# Revit family: E928-1.9_RFA
name_source: partatom
category: Aparatos sanitarios
units: mm (PartAtom-declared; Revit-internal decimal feet)

## family parameters
Compartido = Sí
Corte con vacíos al cargar = No
Cota de conector redondo = Diámetro de uso
Número OmniClass = 23.45.55.14
Punto de cálculo de habitación = Sí
Se basa en plano de trabajo = Sí
Siempre vertical = Sí
Tipo de pieza = Normal
Título OmniClass = Single Faucets

## types (2) — shared parameters
Accesorios = Conectores ½ -14 NPSM
Altura Total = 6"
Anchura Total = 2"
Características del Producto = Monomando tubular para lavabo.
Cartucho = Cartucho Ø25 mm con vástago metálico.
Chrome = Brass
Comentarios de tipo = Monomando tubular para lavabo sin contra.
Cuerpo de Latón = Brass
Elevación por defecto = 1"
Fabricante = HELVEX S.A. de C.V.
Garantía = El producto HELVEX está garantizado como libre de defectos en materiales y procesos de fabricación. El producto HELVEX está garantizado, en lo que se refiere a los acabados; por un periodo de 10 años en los acabados cromo y duravex, y por 2 años en acabados diferentes al cromo, a partir de la fecha de compra indicada en la factura.
Imagen de tipo = E-928.jpg
Instalación = Conexión ½ - 14 NPSM
Operación = El maneral tienen una rotación horizontal para la función de agua caliente y fría; y vertical para abrir y cerrar el flujo de agua.
Presión Máxima de Trabajo = 85.3 psi
Profundidad Total = 5"

## per-type parameters (varying)
| type | Descripción | Modelo | Presión Mínima de Trabajo | URL |
| E-928 | Monomando Century E-928 | E-928 | 5.6 psi | http://www.helvex.com.mx |
| E928-1.9 | Monomando Century E928-1.9 | E-928-1.9 | 8.5 psi | https://www.helvex.com.mx |

## geometry (parser evidence)
native form markers: Sweep x3
no freeform markers — native parametric forms only
